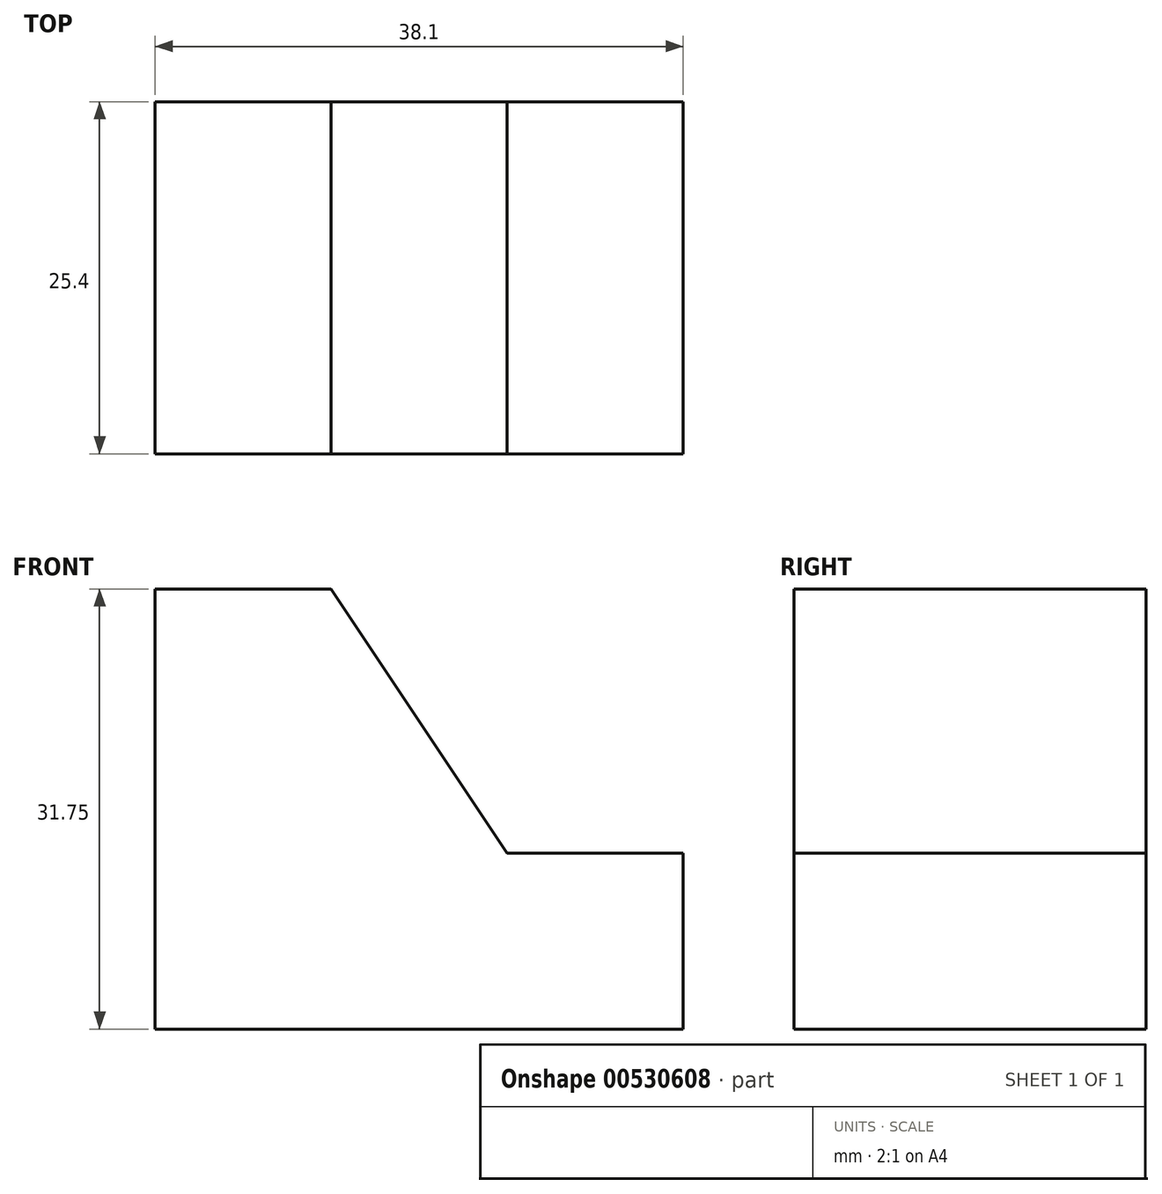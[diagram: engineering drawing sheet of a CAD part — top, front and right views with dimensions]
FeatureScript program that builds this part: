
annotation { "Feature Type Name" : "Feature", "Feature Type Description" : "" }
export const myFeature = defineFeature(function(context is Context, id is Id, definition is map)
    precondition{}
    {
        {
            var Q0;
            Q0=qCreatedBy(makeId("Front.planeOp"),FACE);
            var sketch = newSketch(context, id + "F0", { "sketchPlane" : qUnion([Q0])});
            skLineSegment(sketch, "E0", {"start": v(-54.85, 37.59) * mm, "end": v(-54.85, 5.84) * mm});
            skLineSegment(sketch, "E1", {"start": v(-54.85, 5.84) * mm, "end": v(-16.75, 5.84) * mm});
            skLineSegment(sketch, "E2", {"start": v(-16.75, 5.84) * mm, "end": v(-16.75, 18.54) * mm});
            skLineSegment(sketch, "E3", {"start": v(-29.45, 18.54) * mm, "end": v(-16.75, 18.54) * mm});
            skLineSegment(sketch, "E4", {"start": v(-29.45, 18.54) * mm, "end": v(-42.15, 37.59) * mm});
            skLineSegment(sketch, "E5", {"start": v(-54.85, 37.59) * mm, "end": v(-42.15, 37.59) * mm});
            skSolve(sketch);
        }
        {
            var Q0;
            Q0=makeQuery(id+"F0.imprint","IMPRINT",FACE,{"disambiguationData":[TD([[makeQuery(id+"F0.imprint","IMPRINT",EDGE,{"derivedFrom":sQuery(id+"F0.wireOp",EDGE,"E0")}),1.0]])]});
            extrude(context, id + "F1", {"entities" : qUnion([Q0]), "depth" : 25.4 * mm, "offsetDistance" : 25.4 * mm});
        }
    });
